# Revit family: Kohler Strayt 37327A-4ND-CP Family
name_source: partatom
category: Plumbing Fixtures
revit_build: Autodesk Revit 2018 (Build: 20170223_1515(x64)
units: mm (PartAtom-declared; Revit-internal decimal feet)

## family parameters
Always vertical = Yes
Cut with Voids When Loaded = No
Part Type = Normal
Room Calculation Point = No
Round Connector Dimension = Use Diameter
Shared = No
Work Plane-Based = No

## types (1)
- Kohler Strayt 37327A-4ND-CP
    Cold Water Connection = 6 mm  [stored 0.019685 ft]
    Depth = 141 mm
    Disclaimer = Although care has been taken to ensure, to the best of our knowledge, that all data and information contained herein is accurate to the extent that it relates to either matters of fact or accepted practice at the time of issue. MDFC (Pty) Ltd assumes no responsibility for any errors in, or misinterpretation of, such data and/ or information or any loss or damage arising from, or related to its use.
    Faucet = 40 mm  [stored 0.131234 ft]
    Height = 177 mm
    Hot Water Connection = 6 mm  [stored 0.019685 ft]
    Manufacturer = Kohler Co.
    Material = Chrome
    Model = Kohler Strayt 37327A-4ND-CP
    Telephone = 011 050 9000
    URL = www.africa.kohler.com

note: [stored X ft] marks values corroborated as IEEE doubles in the binary element streams (Revit-internal decimal feet)

## geometry (parser evidence)
native form markers: Blend x2, Sweep x3
no freeform markers — native parametric forms only
